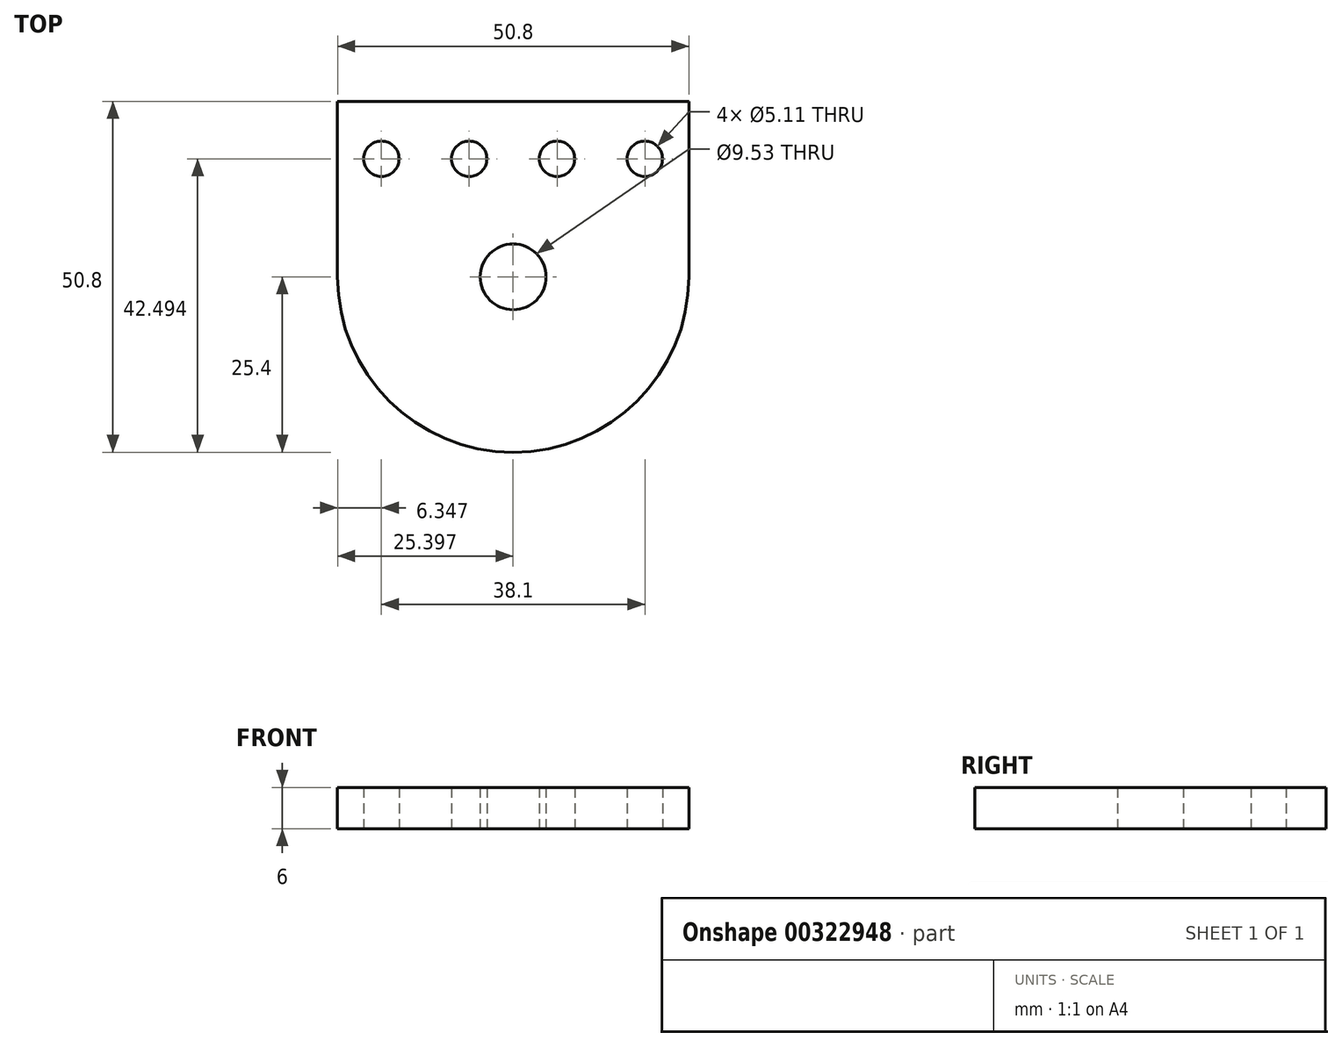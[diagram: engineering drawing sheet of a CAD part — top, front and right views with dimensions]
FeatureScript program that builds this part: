
annotation { "Feature Type Name" : "Feature", "Feature Type Description" : "" }
export const myFeature = defineFeature(function(context is Context, id is Id, definition is map)
    precondition{}
    {
        {
            var Q0;
            Q0=qCreatedBy(makeId("Top.planeOp"),FACE);
            var sketch = newSketch(context, id + "F0", { "sketchPlane" : qUnion([Q0])});
            skLineSegment(sketch, "E0", {"start": v(-30.35, 0) * mm, "end": v(-30.35, -25.4) * mm});
            skLineSegment(sketch, "E1", {"start": v(20.45, 0) * mm, "end": v(20.45, -25.4) * mm});
            skArc(sketch, "E2", {"start": v(-30.35, -25.4) * mm, "mid": v(-4.95, -50.8) * mm, "end": v(20.45, -25.4) * mm});
            skCircle(sketch, "E3", {"center": v(-4.95, -25.4) * mm, "radius": 4.76 * mm});
            skLineSegment(sketch, "E4", {"start": v(-30.35, 0) * mm, "end": v(20.45, 0) * mm});
            skLineSegment(sketch, "E5", {"start": v(-5.57, -20.68) * mm, "end": v(20.45, -20.68) * mm, "construction": true});
            skLineSegment(sketch, "E6", {"start": v(-5.57, -20.68) * mm, "end": v(-30.35, -20.68) * mm, "construction": true});
            skCircle(sketch, "E7.2.0.0", {"center": v(52.2, -12.7) * mm, "radius": 2.55 * mm});
            skLineSegment(sketch, "E8", {"start": v(-4.95, -25.4) * mm, "end": v(-4.95, -0.97) * mm, "construction": true});
            skCircle(sketch, "E9", {"center": v(-11.3, -8.3) * mm, "radius": 2.55 * mm});
            skCircle(sketch, "E10.MirrorC", {"center": v(1.4, -8.3) * mm, "radius": 2.55 * mm});
            skCircle(sketch, "E11.1.0.0", {"center": v(-24, -8.3) * mm, "radius": 2.55 * mm});
            skLineSegment(sketch, "E11.direction1", {"start": v(-11.3, -8.3) * mm, "end": v(-24, -8.3) * mm, "construction": true});
            skCircle(sketch, "E12.1.0.0", {"center": v(14.1, -8.3) * mm, "radius": 2.55 * mm});
            skLineSegment(sketch, "E12.direction1", {"start": v(1.4, -8.3) * mm, "end": v(14.1, -8.3) * mm, "construction": true});
            skSolve(sketch);
        }
        {
            var Q0;
            Q0=makeQuery(id+"F0.imprint","IMPRINT",FACE,{"disambiguationData":[TD([[makeQuery(id+"F0.imprint","IMPRINT",EDGE,{"derivedFrom":sQuery(id+"F0.wireOp",EDGE,"E0")}),1.0]])]});
            extrude(context, id + "F1", {"entities" : qUnion([Q0]), "depth" : 6 * mm});
        }
    });
